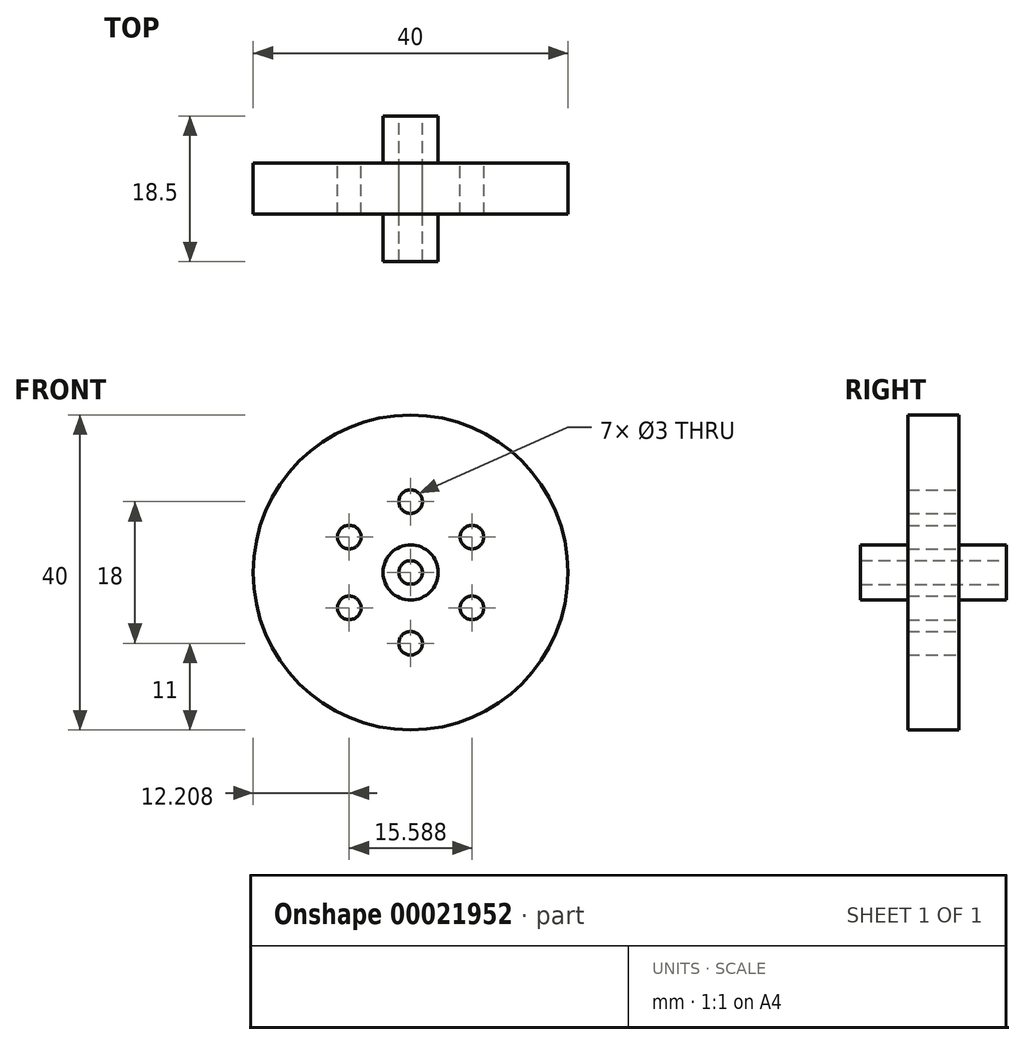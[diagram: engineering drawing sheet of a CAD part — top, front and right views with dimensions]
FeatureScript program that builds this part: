
annotation { "Feature Type Name" : "Feature", "Feature Type Description" : "" }
export const myFeature = defineFeature(function(context is Context, id is Id, definition is map)
    precondition{}
    {
        {
            var Q0;
            Q0=qCreatedBy(makeId("Front.planeOp"),FACE);
            var sketch = newSketch(context, id + "F0", { "sketchPlane" : qUnion([Q0])});
            skCircle(sketch, "E0", {"center": v(36.65, 26.67) * mm, "radius": 20 * mm});
            skCircle(sketch, "E1", {"center": v(36.65, 26.67) * mm, "radius": 1.5 * mm});
            skCircle(sketch, "E2", {"center": v(36.65, 26.67) * mm, "radius": 3.5 * mm});
            skLineSegment(sketch, "E3", {"start": v(36.65, 28.17) * mm, "end": v(36.65, 35.67) * mm});
            skCircle(sketch, "E4", {"center": v(36.65, 35.67) * mm, "radius": 1.5 * mm});
            skCircle(sketch, "E5.1.0", {"center": v(28.86, 31.17) * mm, "radius": 1.5 * mm});
            skCircle(sketch, "E5.2.0", {"center": v(28.86, 22.17) * mm, "radius": 1.5 * mm});
            skCircle(sketch, "E5.3.0", {"center": v(36.65, 17.67) * mm, "radius": 1.5 * mm});
            skCircle(sketch, "E5.4.0", {"center": v(44.45, 22.17) * mm, "radius": 1.5 * mm});
            skCircle(sketch, "E5.5.0", {"center": v(44.45, 31.17) * mm, "radius": 1.5 * mm});
            skSolve(sketch);
        }
        {
            var Q0;
            Q0 = qSketchRegion(id + "F0", true);
            var Q1;
            Q1=makeQuery(id+"F0.imprint","IMPRINT",FACE,{"disambiguationData":[TD([[makeQuery(id+"F0.imprint","IMPRINT",EDGE,{"derivedFrom":sQuery(id+"F0.wireOp",EDGE,"E0")}),1.0]])]});
            extrude(context, id + "F1", {"entities" : qUnion([Q0, Q1]), "depth" : 6.5 * mm});
        }
        {
            var Q0;
            Q0=makeQuery(id+"F0.imprint","IMPRINT",FACE,{"disambiguationData":[TD([[makeQuery(id+"F0.imprint","IMPRINT",EDGE,{"derivedFrom":sQuery(id+"F0.wireOp",EDGE,"E1")}),-1.0]])]});
            extrude(context, id + "F2", {"entities" : qUnion([Q0]), "operationType" : NewBodyOperationType.ADD, "depth" : 12.5 * mm});
        }
        {
            var Q0;
            Q0=makeQuery(id+"F0.imprint","IMPRINT",FACE,{"disambiguationData":[TD([[makeQuery(id+"F0.imprint","IMPRINT",EDGE,{"derivedFrom":sQuery(id+"F0.wireOp",EDGE,"E1")}),-1.0]])]});
            extrude(context, id + "F3", {"entities" : qUnion([Q0]), "operationType" : NewBodyOperationType.ADD, "oppositeDirection" : true, "depth" : 6 * mm});
        }
    });
